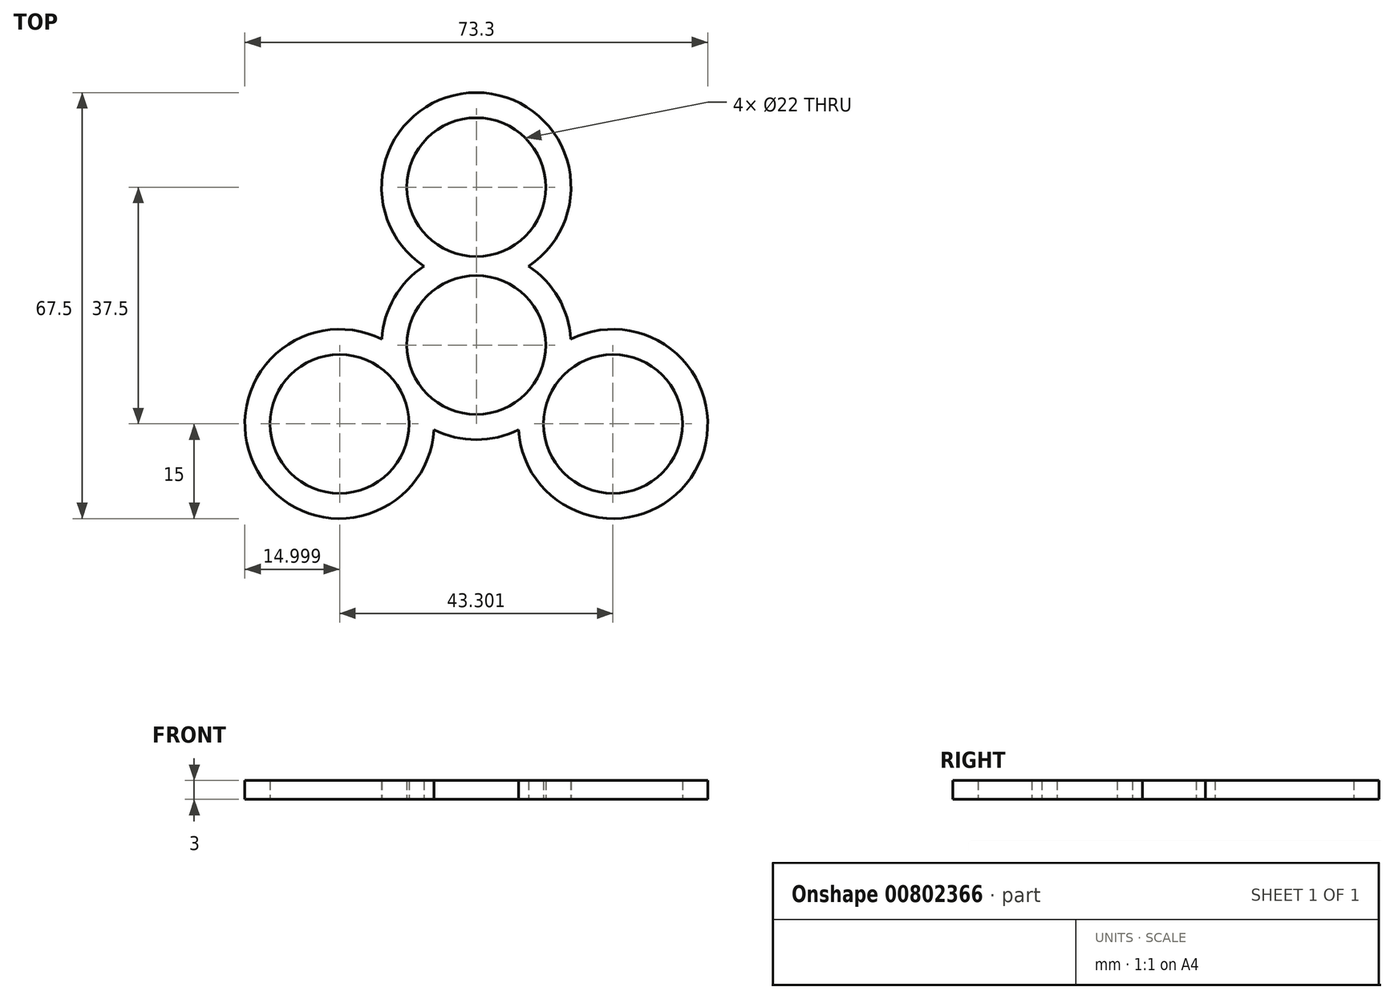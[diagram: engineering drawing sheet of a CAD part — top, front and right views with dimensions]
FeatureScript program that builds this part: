
annotation { "Feature Type Name" : "Feature", "Feature Type Description" : "" }
export const myFeature = defineFeature(function(context is Context, id is Id, definition is map)
    precondition{}
    {
        {
            var Q0;
            Q0=qCreatedBy(makeId("Top.planeOp"),FACE);
            var sketch = newSketch(context, id + "F0", { "sketchPlane" : qUnion([Q0])});
            skArc(sketch, "E0", {"start": v(9.53, 5.5) * mm, "mid": v(0, 11) * mm, "end": v(-9.53, 5.5) * mm});
            skCircle(sketch, "E1", {"center": v(0, 25) * mm, "radius": 11 * mm});
            skArc(sketch, "E2", {"start": v(8.3, 12.5) * mm, "mid": v(0, 40) * mm, "end": v(-8.3, 12.5) * mm});
            skArc(sketch, "E3", {"start": v(-8.3, 12.5) * mm, "mid": v(-10.93, 10.27) * mm, "end": v(-13, 7.5) * mm});
            skArc(sketch, "E4.trimOffspring", {"start": v(13, 7.5) * mm, "mid": v(10.93, 10.27) * mm, "end": v(8.3, 12.5) * mm});
            skArc(sketch, "E5.1.0", {"start": v(-14.97, 0.93) * mm, "mid": v(-34.64, -20) * mm, "end": v(-6.68, -13.43) * mm});
            skCircle(sketch, "E5.1.1", {"center": v(-21.65, -12.5) * mm, "radius": 11 * mm});
            skArc(sketch, "E5.1.2", {"start": v(-13, 7.5) * mm, "mid": v(-14.36, 4.33) * mm, "end": v(-14.97, 0.93) * mm});
            skArc(sketch, "E5.1.3", {"start": v(-9.53, 5.5) * mm, "mid": v(-9.53, -5.5) * mm, "end": v(0, -11) * mm});
            skArc(sketch, "E5.1.4", {"start": v(-6.68, -13.43) * mm, "mid": v(-3.43, -14.6) * mm, "end": v(0, -15) * mm});
            skArc(sketch, "E5.2.0", {"start": v(6.68, -13.43) * mm, "mid": v(34.64, -20) * mm, "end": v(14.97, 0.93) * mm});
            skCircle(sketch, "E5.2.1", {"center": v(21.65, -12.5) * mm, "radius": 11 * mm});
            skArc(sketch, "E5.2.2", {"start": v(0, -15) * mm, "mid": v(3.43, -14.6) * mm, "end": v(6.68, -13.43) * mm});
            skArc(sketch, "E5.2.3", {"start": v(0, -11) * mm, "mid": v(9.53, -5.5) * mm, "end": v(9.53, 5.5) * mm});
            skArc(sketch, "E5.2.4", {"start": v(14.97, 0.93) * mm, "mid": v(14.36, 4.33) * mm, "end": v(13, 7.5) * mm});
            skSolve(sketch);
        }
        {
            var Q0;
            Q0 = qSketchRegion(id + "F0", true);
            extrude(context, id + "F1", {"entities" : qUnion([Q0]), "depth" : 3 * mm, "offsetDistance" : 25 * mm});
        }
    });
